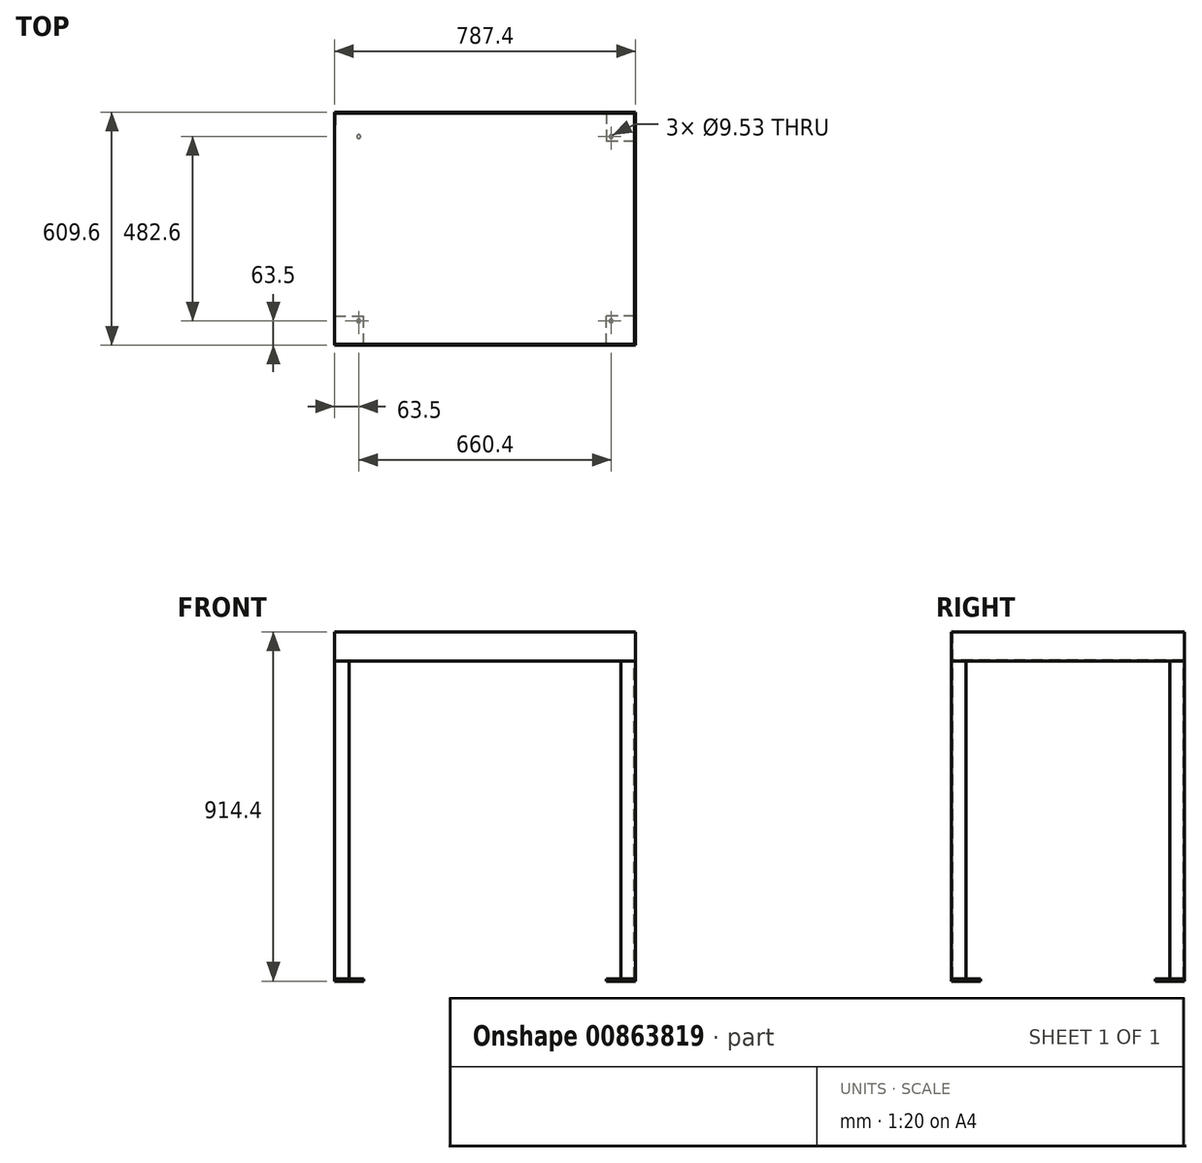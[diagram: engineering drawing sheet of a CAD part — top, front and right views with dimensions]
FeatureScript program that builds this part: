
annotation { "Feature Type Name" : "Feature", "Feature Type Description" : "" }
export const myFeature = defineFeature(function(context is Context, id is Id, definition is map)
    precondition{}
    {
        {
            var Q0;
            Q0=qCreatedBy(makeId("Top.planeOp"),FACE);
            var sketch = newSketch(context, id + "F0", { "sketchPlane" : qUnion([Q0])});
            skLineSegment(sketch, "E0.bottom", {"start": v(-393.7, 304.8) * mm, "end": v(393.7, 304.8) * mm});
            skLineSegment(sketch, "E0.top", {"start": v(-393.7, -304.8) * mm, "end": v(393.7, -304.8) * mm});
            skLineSegment(sketch, "E0.left", {"start": v(-393.7, 304.8) * mm, "end": v(-393.7, -304.8) * mm});
            skLineSegment(sketch, "E0.right", {"start": v(393.7, 304.8) * mm, "end": v(393.7, -304.8) * mm});
            skPoint(sketch, "E0.middle", {"position": v(0, 0) * mm});
            skSolve(sketch);
        }
        {
            var Q0;
            Q0=makeQuery(id+"F0.imprint","IMPRINT",FACE,{"disambiguationData":[TD([[makeQuery(id+"F0.imprint","IMPRINT",EDGE,{"derivedFrom":sQuery(id+"F0.wireOp",EDGE,"E0.bottom")}),-1.0]])]});
            extrude(context, id + "F1", {"entities" : qUnion([Q0]), "depth" : 76.2 * mm, "offsetDistance" : 25.4 * mm});
        }
        {
            var Q0;
            Q0=makeQuery(id+"F1.opExtrude","CAP_FACE",FACE,{"disambiguationData":[OSD([sQuery(id+"F0.wireOp",EDGE,"E0.bottom"),sQuery(id+"F0.wireOp",EDGE,"E0.top"),sQuery(id+"F0.wireOp",EDGE,"E0.left"),sQuery(id+"F0.wireOp",EDGE,"E0.right")])],"isStart":false});
            shell(context, id + "F2", {"entities" : qUnion([Q0]), "thickness" : 2.54 * mm});
        }
        {
            var Q0;
            Q0=makeQuery(id+"F2.opShell","OFFSET_FACE",FACE,{"disambiguationData":[OSD([sQuery(id+"F0.wireOp",EDGE,"E0.left")])]});
            var sketch = newSketch(context, id + "F3", { "sketchPlane" : qUnion([Q0])});
            skSolve(sketch);
        }
        {
            var Q0;
            {var subQ0=sQuery(id+"F0.wireOp",EDGE,"E0.left");Q0=makeQuery(id+"F3.imprint","IMPRINT",FACE,{"disambiguationData":[TD([[makeQuery(id+"F3.imprint","IMPRINT",EDGE,{"derivedFrom":makeQuery(id+"F2.opShell","OFFSET_EDGE",EDGE,{"disambiguationData":[OSD([subQ0]),TDD([makeQuery(id+"F1.opExtrude","CAP_EDGE",EDGE,{"disambiguationData":[OSD([subQ0])],"isStart":true})])]})}),-1.0]])]});}
            extrude(context, id + "F4", {"entities" : qUnion([Q0]), "operationType" : NewBodyOperationType.REMOVE, "oppositeDirection" : true, "depth" : 25.4 * mm, "offsetDistance" : 25.4 * mm});
        }
        {
            var Q0;
            Q0=makeQuery(id+"F1.opExtrude","CAP_FACE",FACE,{"disambiguationData":[OSD([sQuery(id+"F0.wireOp",EDGE,"E0.bottom"),sQuery(id+"F0.wireOp",EDGE,"E0.top"),sQuery(id+"F0.wireOp",EDGE,"E0.left"),sQuery(id+"F0.wireOp",EDGE,"E0.right")])],"isStart":true});
            var sketch = newSketch(context, id + "F5", { "sketchPlane" : qUnion([Q0])});
            skLineSegment(sketch, "E1", {"start": v(-393.7, 304.8) * mm, "end": v(-355.6, 304.8) * mm});
            skLineSegment(sketch, "E2", {"start": v(-355.6, 304.8) * mm, "end": v(-355.6, 301.63) * mm});
            skLineSegment(sketch, "E3", {"start": v(-355.6, 301.63) * mm, "end": v(-390.53, 301.63) * mm});
            skLineSegment(sketch, "E4", {"start": v(-390.53, 301.63) * mm, "end": v(-390.53, 266.7) * mm});
            skLineSegment(sketch, "E5", {"start": v(-390.53, 266.7) * mm, "end": v(-393.7, 266.7) * mm});
            skLineSegment(sketch, "E6", {"start": v(-393.7, 266.7) * mm, "end": v(-393.7, 304.8) * mm});
            skLineSegment(sketch, "E7.MirrorCS", {"start": v(355.6, 304.8) * mm, "end": v(355.6, 301.63) * mm});
            skLineSegment(sketch, "E8.MirrorCS", {"start": v(390.53, 266.7) * mm, "end": v(393.7, 266.7) * mm});
            skLineSegment(sketch, "E9.MirrorCS", {"start": v(393.7, 304.8) * mm, "end": v(355.6, 304.8) * mm});
            skLineSegment(sketch, "E10.MirrorCS", {"start": v(393.7, 266.7) * mm, "end": v(393.7, 304.8) * mm});
            skLineSegment(sketch, "E11.MirrorCS", {"start": v(390.53, 301.63) * mm, "end": v(390.53, 266.7) * mm});
            skLineSegment(sketch, "E12.MirrorCS", {"start": v(355.6, 301.63) * mm, "end": v(390.53, 301.63) * mm});
            skLineSegment(sketch, "E13.MirrorCS", {"start": v(355.6, -304.8) * mm, "end": v(355.6, -301.63) * mm});
            skLineSegment(sketch, "E14.MirrorCS", {"start": v(-390.53, -266.7) * mm, "end": v(-393.7, -266.7) * mm});
            skLineSegment(sketch, "E15.MirrorCS", {"start": v(390.53, -266.7) * mm, "end": v(393.7, -266.7) * mm});
            skLineSegment(sketch, "E16.MirrorCS", {"start": v(-393.7, -266.7) * mm, "end": v(-393.7, -304.8) * mm});
            skLineSegment(sketch, "E17.MirrorCS", {"start": v(355.6, -301.63) * mm, "end": v(390.53, -301.63) * mm});
            skLineSegment(sketch, "E18.MirrorCS", {"start": v(390.53, -301.63) * mm, "end": v(390.53, -266.7) * mm});
            skLineSegment(sketch, "E19.MirrorCS", {"start": v(393.7, -304.8) * mm, "end": v(355.6, -304.8) * mm});
            skLineSegment(sketch, "E20.MirrorCS", {"start": v(393.7, -266.7) * mm, "end": v(393.7, -304.8) * mm});
            skLineSegment(sketch, "E21.MirrorCS", {"start": v(-390.53, -301.63) * mm, "end": v(-390.53, -266.7) * mm});
            skLineSegment(sketch, "E22.MirrorCS", {"start": v(-355.6, -304.8) * mm, "end": v(-355.6, -301.63) * mm});
            skLineSegment(sketch, "E23.MirrorCS", {"start": v(-355.6, -301.63) * mm, "end": v(-390.53, -301.63) * mm});
            skLineSegment(sketch, "E24.MirrorCS", {"start": v(-393.7, -304.8) * mm, "end": v(-355.6, -304.8) * mm});
            skSolve(sketch);
        }
        {
            var Q0;
            Q0=makeQuery(id+"F5.imprint","IMPRINT",FACE,{"disambiguationData":[TD([[makeQuery(id+"F5.imprint","IMPRINT",EDGE,{"derivedFrom":sQuery(id+"F5.wireOp",EDGE,"E1")}),-1.0]])]});
            var Q1;
            Q1=makeQuery(id+"F5.imprint","IMPRINT",FACE,{"disambiguationData":[TD([[makeQuery(id+"F5.imprint","IMPRINT",EDGE,{"derivedFrom":sQuery(id+"F5.wireOp",EDGE,"E14.MirrorCS")}),1.0]])]});
            var Q2;
            Q2=makeQuery(id+"F5.imprint","IMPRINT",FACE,{"disambiguationData":[TD([[makeQuery(id+"F5.imprint","IMPRINT",EDGE,{"derivedFrom":sQuery(id+"F5.wireOp",EDGE,"E13.MirrorCS")}),-1.0]])]});
            var Q3;
            Q3=makeQuery(id+"F5.imprint","IMPRINT",FACE,{"disambiguationData":[TD([[makeQuery(id+"F5.imprint","IMPRINT",EDGE,{"derivedFrom":sQuery(id+"F5.wireOp",EDGE,"E7.MirrorCS")}),1.0]])]});
            extrude(context, id + "F6", {"entities" : qUnion([Q0, Q1, Q2, Q3]), "depth" : 831.85 * mm, "offsetDistance" : 25.4 * mm});
        }
        {
            var Q0;
            Q0=makeQuery(id+"F6.opExtrude","CAP_FACE",FACE,{"disambiguationData":[OSD([sQuery(id+"F5.wireOp",EDGE,"E1"),sQuery(id+"F5.wireOp",EDGE,"E2"),sQuery(id+"F5.wireOp",EDGE,"E3"),sQuery(id+"F5.wireOp",EDGE,"E4"),sQuery(id+"F5.wireOp",EDGE,"E5"),sQuery(id+"F5.wireOp",EDGE,"E6")])],"isStart":false});
            var sketch = newSketch(context, id + "F7", { "sketchPlane" : qUnion([Q0])});
            skLineSegment(sketch, "E25.bottom", {"start": v(-393.7, 304.8) * mm, "end": v(-317.5, 304.8) * mm});
            skLineSegment(sketch, "E25.top", {"start": v(-393.7, 228.6) * mm, "end": v(-317.5, 228.6) * mm});
            skLineSegment(sketch, "E25.left", {"start": v(-393.7, 304.8) * mm, "end": v(-393.7, 228.6) * mm});
            skLineSegment(sketch, "E25.right", {"start": v(-317.5, 304.8) * mm, "end": v(-317.5, 228.6) * mm});
            skLineSegment(sketch, "E26.MirrorCS", {"start": v(393.7, 228.6) * mm, "end": v(317.5, 228.6) * mm});
            skLineSegment(sketch, "E27.MirrorCS", {"start": v(393.7, 304.8) * mm, "end": v(393.7, 228.6) * mm});
            skLineSegment(sketch, "E28.MirrorCS", {"start": v(317.5, 304.8) * mm, "end": v(317.5, 228.6) * mm});
            skLineSegment(sketch, "E29.MirrorCS", {"start": v(393.7, 304.8) * mm, "end": v(317.5, 304.8) * mm});
            skCircle(sketch, "E30", {"center": v(-330.2, 241.3) * mm, "radius": 4.76 * mm});
            skCircle(sketch, "E31.MirrorC", {"center": v(330.2, 241.3) * mm, "radius": 4.76 * mm});
            skCircle(sketch, "E32.MirrorC", {"center": v(-330.2, -241.3) * mm, "radius": 4.76 * mm});
            skLineSegment(sketch, "E33.MirrorCS", {"start": v(393.7, -228.6) * mm, "end": v(317.5, -228.6) * mm});
            skLineSegment(sketch, "E34.MirrorCS", {"start": v(393.7, -304.8) * mm, "end": v(393.7, -228.6) * mm});
            skLineSegment(sketch, "E35.MirrorCS", {"start": v(393.7, -304.8) * mm, "end": v(317.5, -304.8) * mm});
            skCircle(sketch, "E36.MirrorC", {"center": v(330.2, -241.3) * mm, "radius": 4.76 * mm});
            skLineSegment(sketch, "E37.MirrorCS", {"start": v(317.5, -304.8) * mm, "end": v(317.5, -228.6) * mm});
            skLineSegment(sketch, "E38.MirrorCS", {"start": v(-393.7, -304.8) * mm, "end": v(-317.5, -304.8) * mm});
            skLineSegment(sketch, "E39.MirrorCS", {"start": v(-317.5, -304.8) * mm, "end": v(-317.5, -228.6) * mm});
            skLineSegment(sketch, "E40.MirrorCS", {"start": v(-393.7, -304.8) * mm, "end": v(-393.7, -228.6) * mm});
            skLineSegment(sketch, "E41.MirrorCS", {"start": v(-393.7, -228.6) * mm, "end": v(-317.5, -228.6) * mm});
            skSolve(sketch);
        }
        {
            var Q0;
            {var subQ3=sQuery(id+"F7.wireOp",EDGE,"E25.top");Q0=makeQuery(id+"F7.imprint","IMPRINT",FACE,{"disambiguationData":[TD([[makeQuery(id+"F7.imprint","IMPRINT",EDGE,{"derivedFrom":subQ3}),1.0]])]});}
            var Q1;
            Q1=makeQuery(id+"F7.imprint","IMPRINT",FACE,{"disambiguationData":[TD([[makeQuery(id+"F7.imprint","IMPRINT",EDGE,{"derivedFrom":sQuery(id+"F7.wireOp",EDGE,"E32.MirrorC")}),1.0]])]});
            var Q2;
            Q2=makeQuery(id+"F7.imprint","IMPRINT",FACE,{"disambiguationData":[TD([[makeQuery(id+"F7.imprint","IMPRINT",EDGE,{"derivedFrom":sQuery(id+"F7.wireOp",EDGE,"E36.MirrorC")}),-1.0]])]});
            var Q3;
            Q3=makeQuery(id+"F7.imprint","IMPRINT",FACE,{"disambiguationData":[TD([[makeQuery(id+"F7.imprint","IMPRINT",EDGE,{"derivedFrom":sQuery(id+"F7.wireOp",EDGE,"E26.MirrorCS")}),-1.0]])]});
            var Q4;
            {var subQ0=makeQuery(id+"F6.opExtrude","CAP_EDGE",EDGE,{"disambiguationData":[OSD([sQuery(id+"F5.wireOp",EDGE,"E2")])],"isStart":false});Q4=makeQuery(id+"F7.imprint","IMPRINT",FACE,{"disambiguationData":[TD([[makeQuery(id+"F7.imprint","IMPRINT",EDGE,{"derivedFrom":subQ0}),-1.0]])]});}
            extrude(context, id + "F8", {"entities" : qUnion([Q0, Q1, Q2, Q3, Q4]), "depth" : 6.35 * mm, "offsetDistance" : 25.4 * mm});
        }
    });
